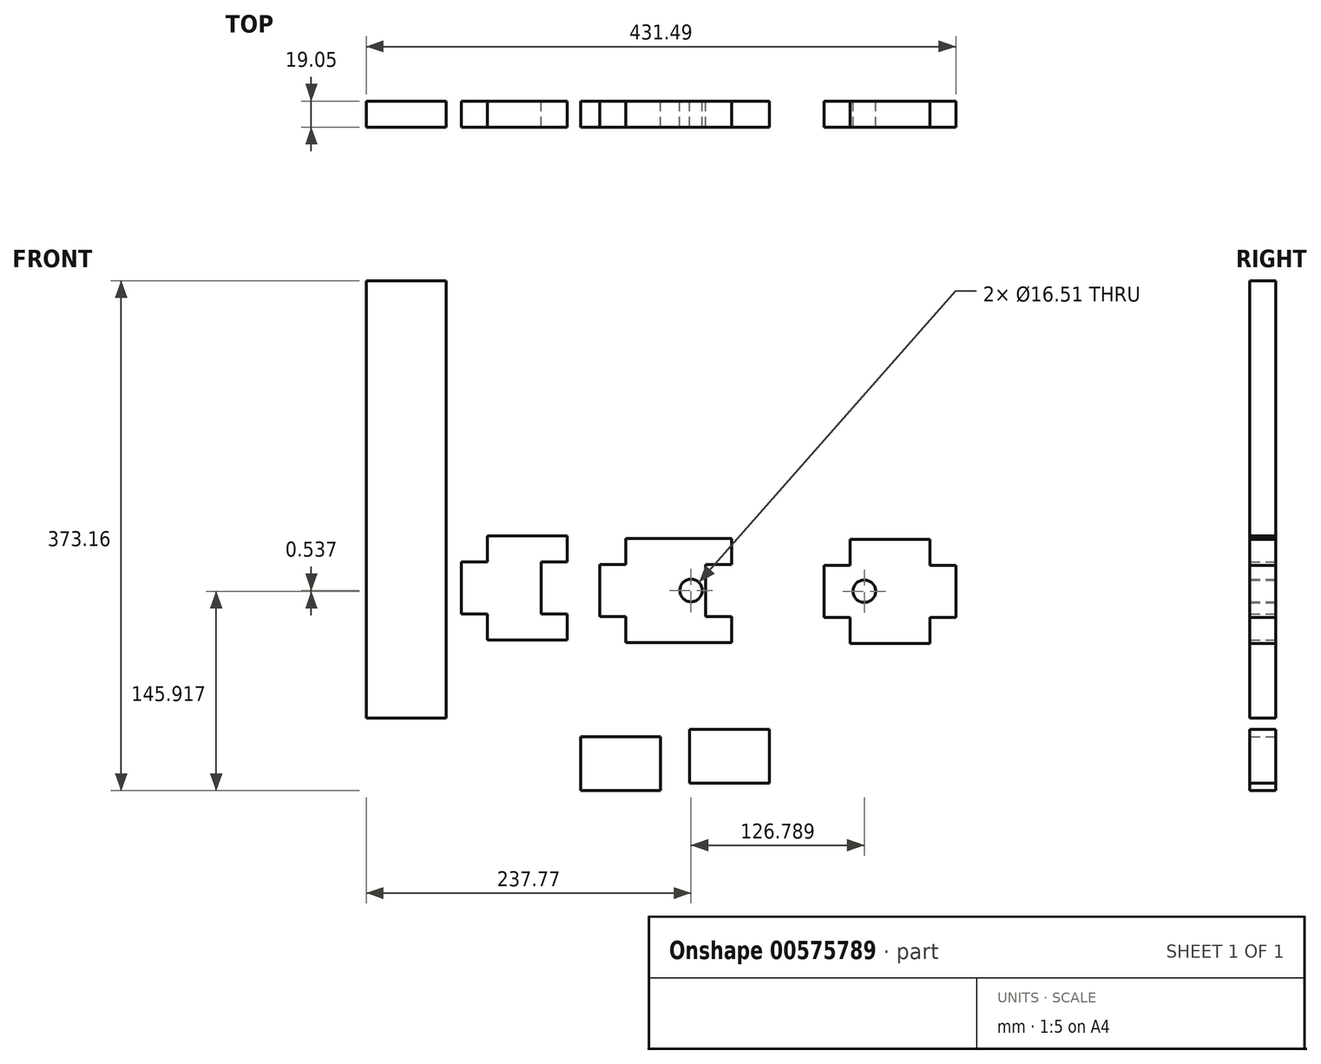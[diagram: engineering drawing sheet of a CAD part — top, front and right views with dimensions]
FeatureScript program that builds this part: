
annotation { "Feature Type Name" : "Feature", "Feature Type Description" : "" }
export const myFeature = defineFeature(function(context is Context, id is Id, definition is map)
    precondition{}
    {
        {
            var Q0;
            Q0=qCreatedBy(makeId("Front.planeOp"),FACE);
            var sketch = newSketch(context, id + "F0", { "sketchPlane" : qUnion([Q0])});
            skLineSegment(sketch, "E0", {"start": v(-42.28, 44.71) * mm, "end": v(35.2, 44.71) * mm});
            skLineSegment(sketch, "E1", {"start": v(35.2, -31.49) * mm, "end": v(-42.28, -31.49) * mm});
            skLineSegment(sketch, "E2", {"start": v(-232.17, -86.72) * mm, "end": v(-173.75, -86.72) * mm});
            skLineSegment(sketch, "E3", {"start": v(-173.75, -86.72) * mm, "end": v(-173.75, 233.32) * mm});
            skLineSegment(sketch, "E4", {"start": v(-173.75, 233.32) * mm, "end": v(-232.17, 233.32) * mm});
            skLineSegment(sketch, "E5", {"start": v(-232.17, 233.32) * mm, "end": v(-232.17, -86.72) * mm});
            skLineSegment(sketch, "E6", {"start": v(-42.28, -31.49) * mm, "end": v(-42.28, -12.44) * mm});
            skLineSegment(sketch, "E7", {"start": v(-42.28, 25.66) * mm, "end": v(-42.28, 44.71) * mm});
            skLineSegment(sketch, "E8", {"start": v(35.2, -31.49) * mm, "end": v(35.2, -12.44) * mm});
            skLineSegment(sketch, "E9", {"start": v(35.2, -12.44) * mm, "end": v(16.14, -12.44) * mm});
            skLineSegment(sketch, "E10", {"start": v(16.14, -12.44) * mm, "end": v(16.14, 25.66) * mm});
            skLineSegment(sketch, "E11", {"start": v(16.14, 25.66) * mm, "end": v(35.2, 25.66) * mm});
            skLineSegment(sketch, "E12", {"start": v(35.2, 25.66) * mm, "end": v(35.2, 44.71) * mm});
            skCircle(sketch, "E13", {"center": v(5.6, 6.61) * mm, "radius": 8.26 * mm});
            skLineSegment(sketch, "E14", {"start": v(-143.38, 46.6) * mm, "end": v(-84.96, 46.6) * mm});
            skLineSegment(sketch, "E15", {"start": v(-84.96, -29.6) * mm, "end": v(-143.38, -29.6) * mm});
            skLineSegment(sketch, "E16", {"start": v(-143.38, -29.6) * mm, "end": v(-143.38, -10.55) * mm});
            skLineSegment(sketch, "E17", {"start": v(-143.38, -10.55) * mm, "end": v(-162.43, -10.55) * mm});
            skLineSegment(sketch, "E18", {"start": v(-162.43, -10.55) * mm, "end": v(-162.43, 27.55) * mm});
            skLineSegment(sketch, "E19", {"start": v(-162.43, 27.55) * mm, "end": v(-143.38, 27.55) * mm});
            skLineSegment(sketch, "E20", {"start": v(-143.38, 27.55) * mm, "end": v(-143.38, 46.6) * mm});
            skLineSegment(sketch, "E21", {"start": v(-84.96, -29.6) * mm, "end": v(-84.96, -10.55) * mm});
            skLineSegment(sketch, "E22", {"start": v(-84.96, -10.55) * mm, "end": v(-104.01, -10.55) * mm});
            skLineSegment(sketch, "E23", {"start": v(-104.01, -10.55) * mm, "end": v(-104.01, 27.55) * mm});
            skLineSegment(sketch, "E24", {"start": v(-104.01, 27.55) * mm, "end": v(-84.96, 27.55) * mm});
            skLineSegment(sketch, "E25", {"start": v(-84.96, 27.55) * mm, "end": v(-84.96, 46.6) * mm});
            skLineSegment(sketch, "E26", {"start": v(121.85, 44.18) * mm, "end": v(180.27, 44.18) * mm});
            skLineSegment(sketch, "E27", {"start": v(180.27, -32.02) * mm, "end": v(121.85, -32.02) * mm});
            skLineSegment(sketch, "E28", {"start": v(121.85, -32.02) * mm, "end": v(121.85, -12.97) * mm});
            skLineSegment(sketch, "E29", {"start": v(121.85, -12.97) * mm, "end": v(102.8, -12.97) * mm});
            skLineSegment(sketch, "E30", {"start": v(102.8, -12.97) * mm, "end": v(102.8, 25.13) * mm});
            skLineSegment(sketch, "E31", {"start": v(102.8, 25.13) * mm, "end": v(121.85, 25.13) * mm});
            skLineSegment(sketch, "E32", {"start": v(121.85, 25.13) * mm, "end": v(121.85, 44.18) * mm});
            skLineSegment(sketch, "E33", {"start": v(180.27, -32.02) * mm, "end": v(180.27, -12.97) * mm});
            skLineSegment(sketch, "E34", {"start": v(180.27, 25.13) * mm, "end": v(180.27, 44.18) * mm});
            skCircle(sketch, "E35", {"center": v(132.39, 6.08) * mm, "radius": 8.26 * mm});
            skLineSegment(sketch, "E36", {"start": v(-75.21, -139.84) * mm, "end": v(-75.21, -100.47) * mm});
            skLineSegment(sketch, "E37", {"start": v(-75.21, -100.47) * mm, "end": v(-16.8, -100.47) * mm});
            skLineSegment(sketch, "E38", {"start": v(-16.8, -100.47) * mm, "end": v(-16.8, -139.84) * mm});
            skLineSegment(sketch, "E39", {"start": v(-16.8, -139.84) * mm, "end": v(-75.21, -139.84) * mm});
            skLineSegment(sketch, "E40", {"start": v(4.5, -134.53) * mm, "end": v(4.5, -95.16) * mm});
            skLineSegment(sketch, "E41", {"start": v(4.5, -95.16) * mm, "end": v(62.92, -95.16) * mm});
            skLineSegment(sketch, "E42", {"start": v(62.92, -95.16) * mm, "end": v(62.92, -134.53) * mm});
            skLineSegment(sketch, "E43", {"start": v(62.92, -134.53) * mm, "end": v(4.5, -134.53) * mm});
            skLineSegment(sketch, "E44", {"start": v(180.27, -12.97) * mm, "end": v(199.32, -12.97) * mm});
            skLineSegment(sketch, "E45", {"start": v(199.32, -12.97) * mm, "end": v(199.32, 25.13) * mm});
            skLineSegment(sketch, "E46", {"start": v(199.32, 25.13) * mm, "end": v(180.27, 25.13) * mm});
            skLineSegment(sketch, "E47", {"start": v(-61.33, -12.44) * mm, "end": v(-61.33, 25.66) * mm});
            skLineSegment(sketch, "E48", {"start": v(-42.28, -12.44) * mm, "end": v(-61.33, -12.44) * mm});
            skLineSegment(sketch, "E49", {"start": v(-61.33, 25.66) * mm, "end": v(-42.28, 25.66) * mm});
            skSolve(sketch);
        }
        {
            var Q0;
            Q0=makeQuery(id+"F0.imprint","IMPRINT",FACE,{"disambiguationData":[TD([[makeQuery(id+"F0.imprint","IMPRINT",EDGE,{"derivedFrom":sQuery(id+"F0.wireOp",EDGE,"E14")}),-1.0]])]});
            var Q1;
            Q1=makeQuery(id+"F0.imprint","IMPRINT",FACE,{"disambiguationData":[TD([[makeQuery(id+"F0.imprint","IMPRINT",EDGE,{"derivedFrom":sQuery(id+"F0.wireOp",EDGE,"E0")}),-1.0]])]});
            var Q2;
            Q2=makeQuery(id+"F0.imprint","IMPRINT",FACE,{"disambiguationData":[TD([[makeQuery(id+"F0.imprint","IMPRINT",EDGE,{"derivedFrom":sQuery(id+"F0.wireOp",EDGE,"20387028-254c-41ed-9181-aeea533c90f1")}),-1.0]])]});
            var Q3;
            Q3=makeQuery(id+"F0.imprint","IMPRINT",FACE,{"disambiguationData":[TD([[makeQuery(id+"F0.imprint","IMPRINT",EDGE,{"derivedFrom":sQuery(id+"F0.wireOp",EDGE,"E26")}),-1.0]])]});
            var Q4;
            Q4=makeQuery(id+"F0.imprint","IMPRINT",FACE,{"disambiguationData":[TD([[makeQuery(id+"F0.imprint","IMPRINT",EDGE,{"derivedFrom":sQuery(id+"F0.wireOp",EDGE,"E36")}),-1.0]])]});
            var Q5;
            Q5=makeQuery(id+"F0.imprint","IMPRINT",FACE,{"disambiguationData":[TD([[makeQuery(id+"F0.imprint","IMPRINT",EDGE,{"derivedFrom":sQuery(id+"F0.wireOp",EDGE,"E40")}),-1.0]])]});
            extrude(context, id + "F1", {"entities" : qUnion([Q0, Q1, Q2, Q3, Q4, Q5]), "depth" : 19.05 * mm, "offsetDistance" : 25.4 * mm});
        }
        {
            var Q0;
            Q0=makeQuery(id+"F0.imprint","IMPRINT",FACE,{"disambiguationData":[TD([[makeQuery(id+"F0.imprint","IMPRINT",EDGE,{"derivedFrom":sQuery(id+"F0.wireOp",EDGE,"E2")}),1.0]])]});
            extrude(context, id + "F2", {"entities" : qUnion([Q0]), "depth" : 19.05 * mm, "offsetDistance" : 25.4 * mm});
        }
    });
